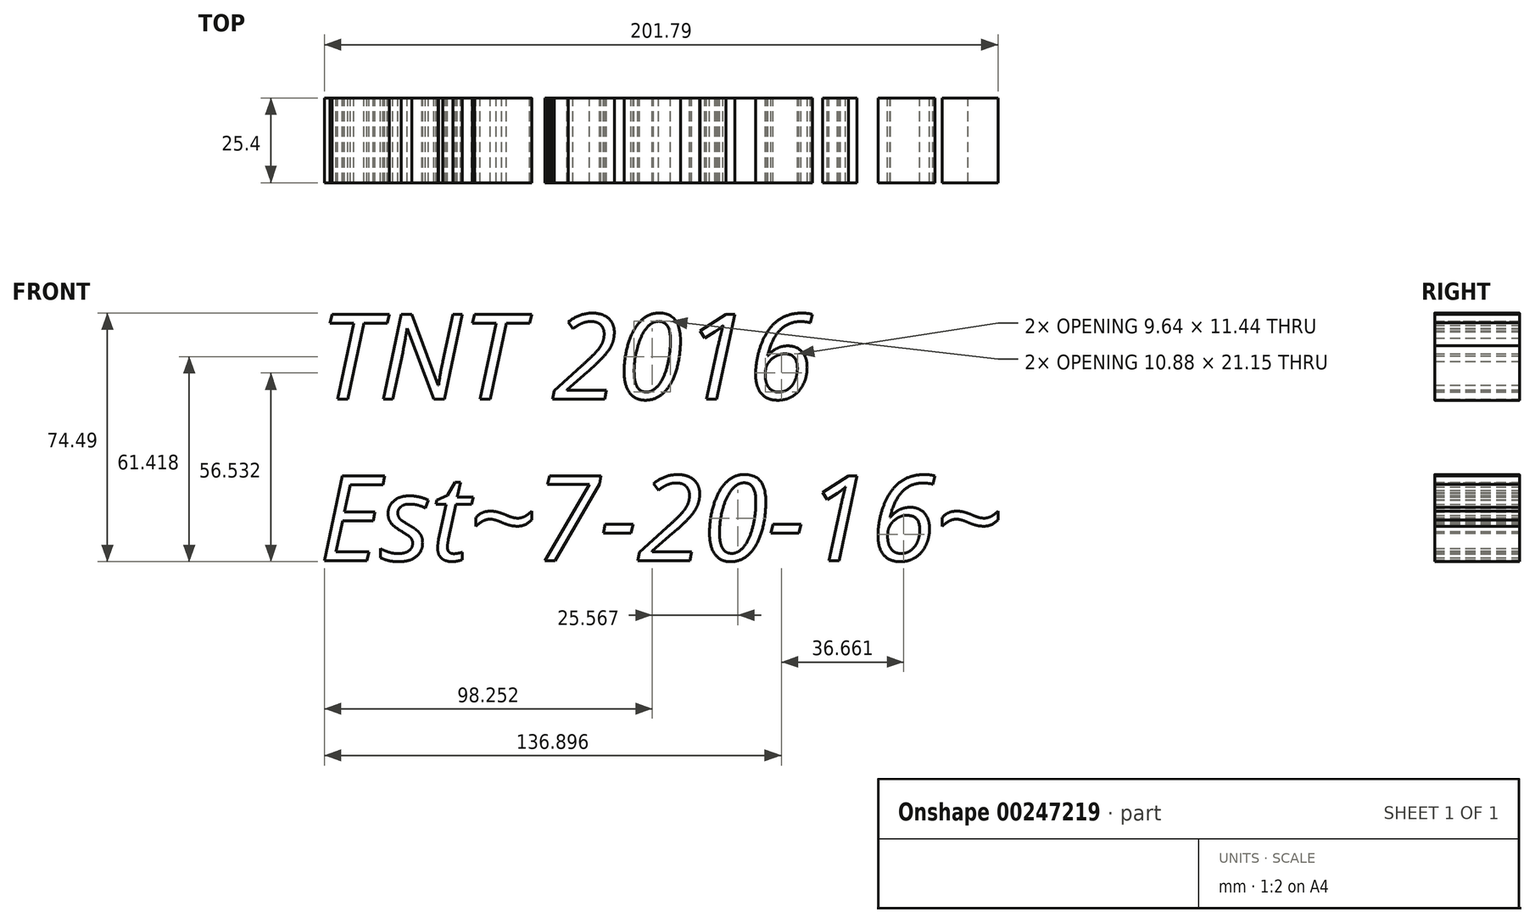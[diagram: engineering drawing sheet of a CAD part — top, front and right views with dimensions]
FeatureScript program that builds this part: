
annotation { "Feature Type Name" : "Feature", "Feature Type Description" : "" }
export const myFeature = defineFeature(function(context is Context, id is Id, definition is map)
    precondition{}
    {
        {
            var Q0;
            Q0=qCreatedBy(makeId("Front.planeOp"),FACE);
            var sketch = newSketch(context, id + "F0", { "sketchPlane" : qUnion([Q0])});
            skText(sketch, "E0", { "text": "TNT 2016 \nEst~7-20-16~", "fontName": "OpenSans-Italic.ttf"});
            const initialGuessF0  = {"E0": [-0.03516, -0.00763, 1, 0, 0.0256]};
            skSetInitialGuess(sketch, initialGuessF0);
            skSolve(sketch);
        }
        {
            var Q0;
            Q0 = qSketchRegion(id + "F0", true);
            extrude(context, id + "F1", {"entities" : qUnion([Q0]), "depth" : 25.4 * mm});
        }
    });
